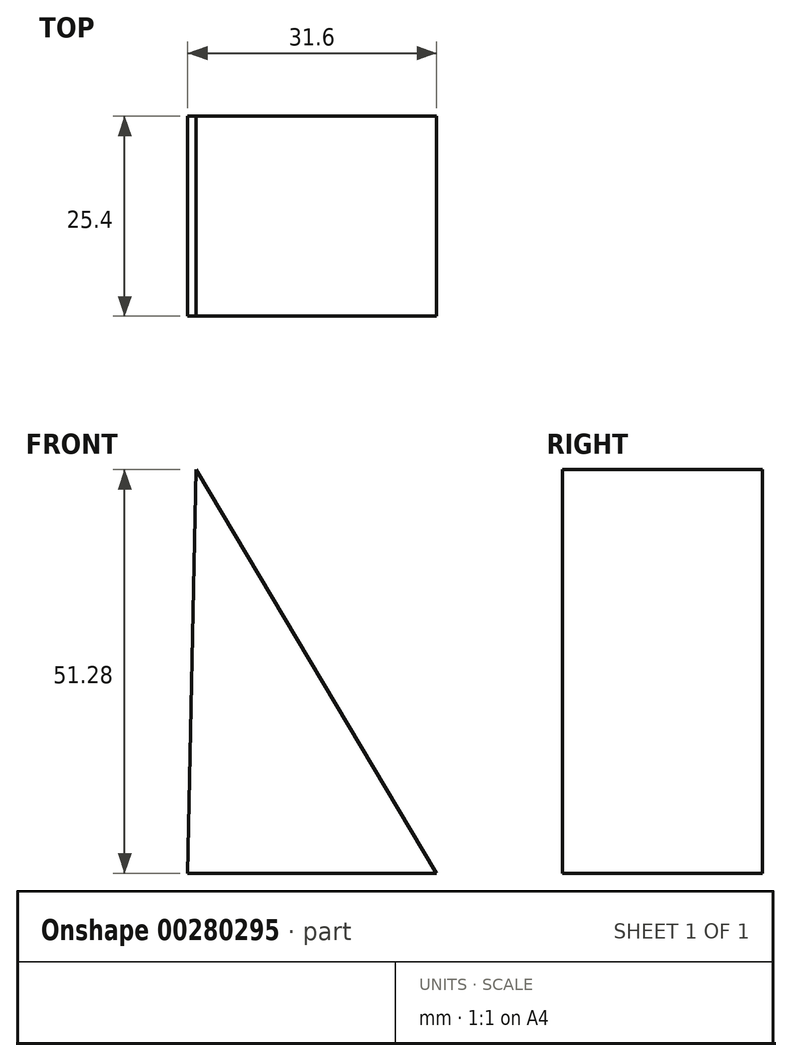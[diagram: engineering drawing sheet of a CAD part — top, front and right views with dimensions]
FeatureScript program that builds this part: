
annotation { "Feature Type Name" : "Feature", "Feature Type Description" : "" }
export const myFeature = defineFeature(function(context is Context, id is Id, definition is map)
    precondition{}
    {
        {
            var Q0;
            Q0=qCreatedBy(makeId("Front.planeOp"),FACE);
            var sketch = newSketch(context, id + "F0", { "sketchPlane" : qUnion([Q0])});
            skLineSegment(sketch, "E0", {"start": v(-31.6, 0) * mm, "end": v(0, 0) * mm});
            skLineSegment(sketch, "E1", {"start": v(0, 0) * mm, "end": v(-30.54, 51.28) * mm});
            skLineSegment(sketch, "E2", {"start": v(-30.54, 51.28) * mm, "end": v(-31.6, 0) * mm});
            skSolve(sketch);
        }
        {
            var Q0;
            Q0 = qSketchRegion(id + "F0", true);
            extrude(context, id + "F1", {"entities" : qUnion([Q0]), "depth" : 25.4 * mm});
        }
    });
